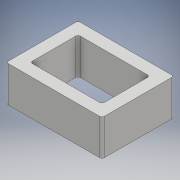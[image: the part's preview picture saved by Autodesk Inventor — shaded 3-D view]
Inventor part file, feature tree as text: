
AUTODESK INVENTOR PART (.ipt)
format: ipt  version: 2017 (Build 210142000, 142)  size: 111,104 bytes
history: native  units: mm
features: fillet x2, extrude x1, sketch x1
ambient origin geometry x8: Origin, YZ Plane, XZ Plane, XY Plane, X Axis, Y Axis, Z Axis, Center Point
bodies: Solid1 (feature_tree)
feature tree (4):
  extrude  "Extrusion1"  Depth=20.0mm
  fillet  "Fillet1"  Radius=40.0mm
  fillet  "Fillet2"  Radius=30.0mm
  sketch  "Sketch1"  dims[d0=30.0mm d1=20.0mm d2=40.0mm d3=30.0mm d4=15.0mm d5=0.0mm d6=1.0mm d7=1.0mm]
